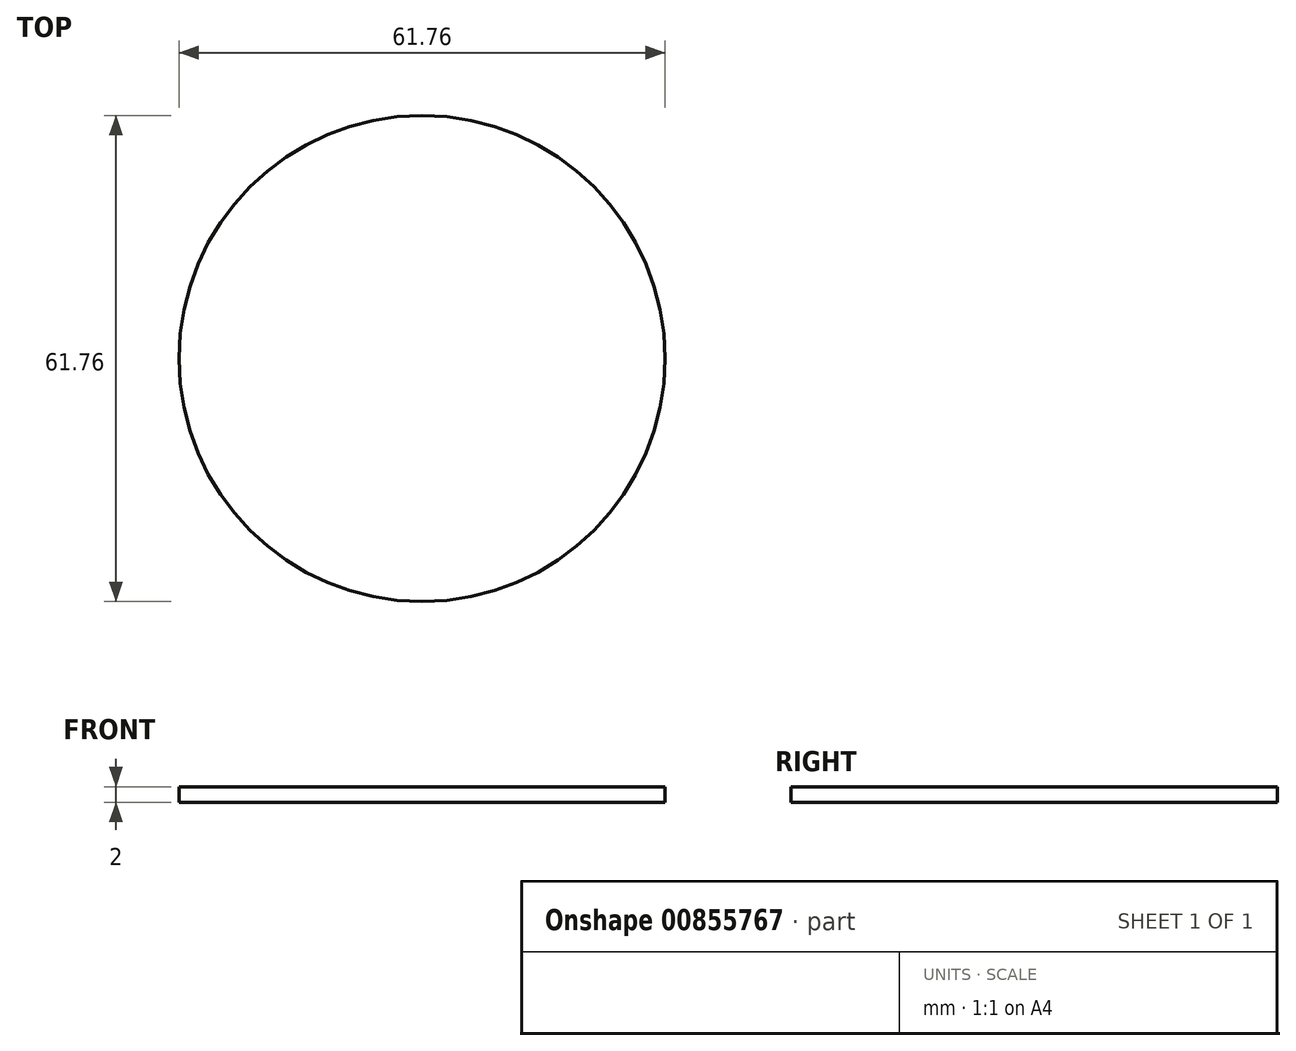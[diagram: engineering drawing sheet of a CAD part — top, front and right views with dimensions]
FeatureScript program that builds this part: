
annotation { "Feature Type Name" : "Feature", "Feature Type Description" : "" }
export const myFeature = defineFeature(function(context is Context, id is Id, definition is map)
    precondition{}
    {
        {
            var Q0;
            Q0=qCreatedBy(makeId("Top.planeOp"),FACE);
            var sketch = newSketch(context, id + "F0", { "sketchPlane" : qUnion([Q0])});
            skCircle(sketch, "E0", {"center": v(0, 0) * mm, "radius": 30.88 * mm});
            skSolve(sketch);
        }
        {
            var Q0;
            Q0=makeQuery(id+"F0.imprint","IMPRINT",FACE,{"disambiguationData":[TD([[makeQuery(id+"F0.imprint","IMPRINT",EDGE,{"derivedFrom":sQuery(id+"F0.wireOp",EDGE,"E0")}),1.0]])]});
            var sketch = newSketch(context, id + "F1", { "sketchPlane" : qUnion([Q0])});
            skSolve(sketch);
        }
        {
            var Q0;
            Q0=makeQuery(id+"F1.imprint","IMPRINT",FACE,{"disambiguationData":[TD([[makeQuery(id+"F1.imprint","IMPRINT",EDGE,{"derivedFrom":makeQuery(id+"F0.imprint","IMPRINT",EDGE,{"derivedFrom":sQuery(id+"F0.wireOp",EDGE,"E0")})}),1.0]])]});
            extrude(context, id + "F2", {"entities" : qUnion([Q0]), "depth" : 2 * mm, "offsetDistance" : 25 * mm});
        }
    });
